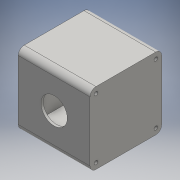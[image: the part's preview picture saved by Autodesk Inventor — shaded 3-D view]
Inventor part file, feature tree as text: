
AUTODESK INVENTOR PART (.ipt)
format: ipt  version: 2016 (Build 200138000, 138)  size: 156,160 bytes
history: native  units: mm
features: extrude x5, sketch x5, fillet x1
ambient origin geometry x8: Origin, YZ Plane, XZ Plane, XY Plane, X Axis, Y Axis, Z Axis, Center Point
bodies: Solid1 (feature_tree)
feature tree (11):
  extrude  "Main Block"  Depth=60.0mm
  extrude  "Motor Void"  Depth=42.0mm
  extrude  "Cable Void"  Depth=58.0mm TaperAngle=0.0deg
  extrude  "Raised Void"  Depth=31.0mm
  extrude  "Holes"  Depth=16.5mm
  fillet  "Cleaning it up"  Radius=9.0mm
  sketch  "Sketch1"  dims[d0=60.0mm d1=60.0mm]
  sketch  "Sketch2"  dims[d2=60.0mm d3=0.0mm d4=42.0mm]
  sketch  "Sketch3"  dims[d5=42.0mm d6=58.0mm d7=0.0mm]
  sketch  "Sketch4"  dims[d10=31.0mm d11=0.0mm d12=22.0mm]
  sketch  "Sketch6"  dims[d13=2.0mm d14=0.0mm d30=16.5mm d31=9.0mm d32=5.0mm d33=5.0mm d34=5.0mm d35=5.0mm d36=5.0mm d37=5.0mm d38=5.0mm d39=5.0mm d40=3.0mm d41=3.0mm d42=3.0mm d43=3.0mm d44=60.0mm d45=0.0mm d46=5.0mm]
